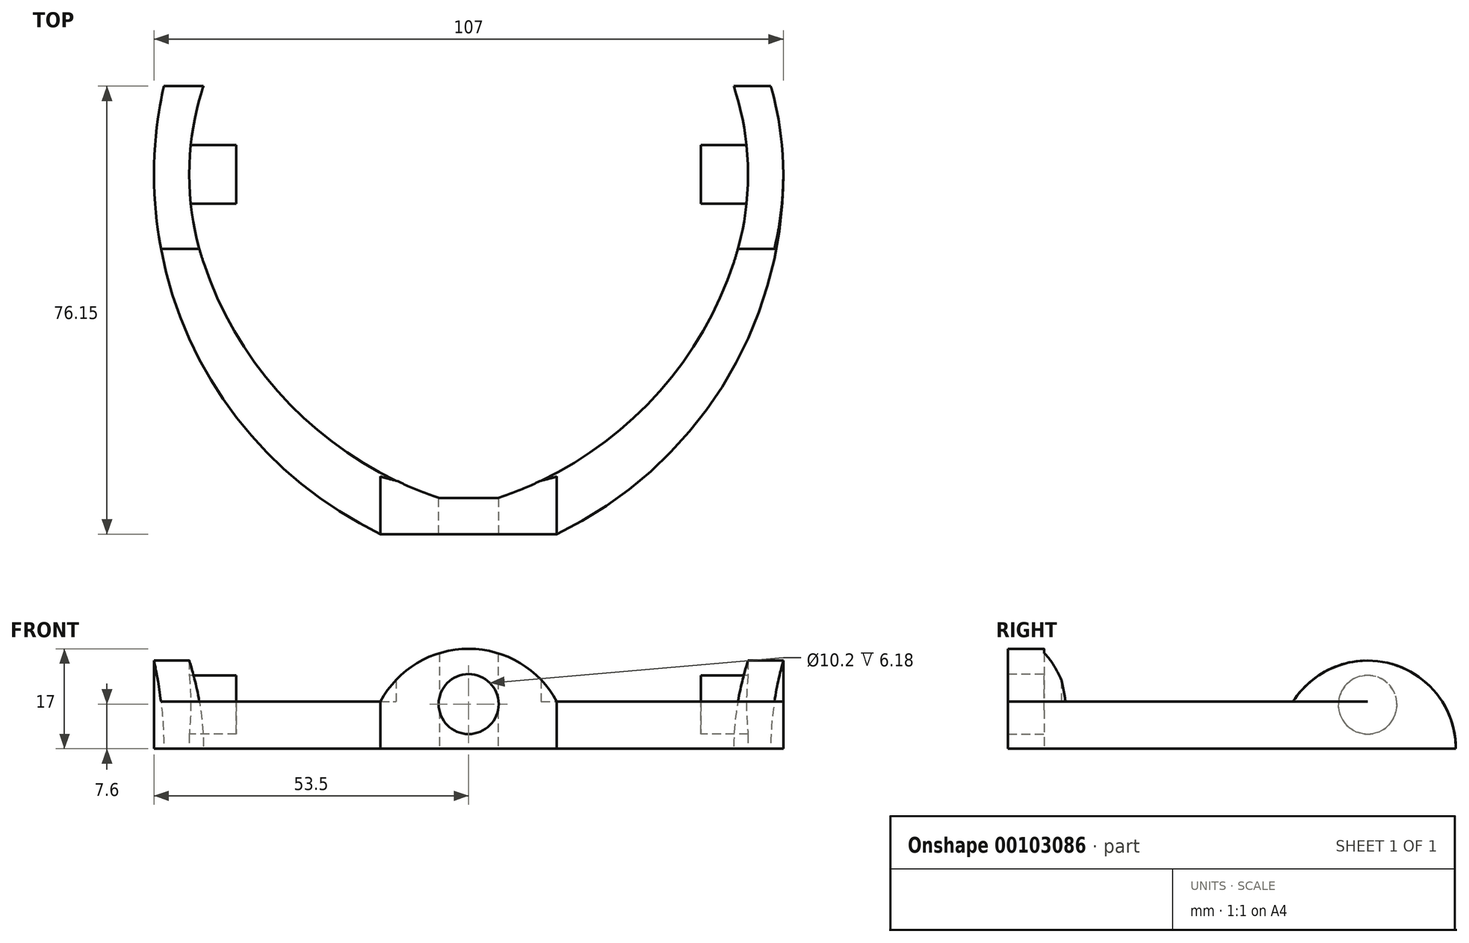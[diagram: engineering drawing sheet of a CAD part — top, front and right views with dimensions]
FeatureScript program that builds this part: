
annotation { "Feature Type Name" : "Feature", "Feature Type Description" : "" }
export const myFeature = defineFeature(function(context is Context, id is Id, definition is map)
    precondition{}
    {
        {
            var Q0;
            Q0=qCreatedBy(makeId("Top.planeOp"),FACE);
            var sketch = newSketch(context, id + "F0", { "sketchPlane" : qUnion([Q0])});
            skCircle(sketch, "E0", {"center": v(0, 0) * mm, "radius": 46 * mm});
            skCircle(sketch, "E1", {"center": v(0, 0) * mm, "radius": 40 * mm});
            skSolve(sketch);
        }
        {
            var Q0;
            Q0=qCreatedBy(makeId("Top.planeOp"),FACE);
            var sketch = newSketch(context, id + "F1", { "sketchPlane" : qUnion([Q0])});
            skArc(sketch, "E2.0", {"start": v(-45.07, 15) * mm, "mid": v(-47.5, 0) * mm, "end": v(-45.07, -15) * mm});
            skArc(sketch, "E3.0", {"start": v(-49.94, 19.18) * mm, "mid": v(-52.6, 9.75) * mm, "end": v(-53.5, 0) * mm});
            skLineSegment(sketch, "E4", {"start": v(0, 0) * mm, "end": v(0, -15) * mm, "construction": true});
            skLineSegment(sketch, "E5", {"start": v(-51.82, -15) * mm, "end": v(51.82, -15) * mm, "construction": true});
            skLineSegment(sketch, "E6", {"start": v(0, -55) * mm, "end": v(0, -65) * mm, "construction": true});
            skLineSegment(sketch, "E7", {"start": v(0, -65) * mm, "end": v(-5, -65) * mm});
            skLineSegment(sketch, "E8", {"start": v(0, -65) * mm, "end": v(5, -65) * mm});
            skArc(sketch, "E9", {"start": v(-53.5, 0) * mm, "mid": v(-53.08, -7.55) * mm, "end": v(-51.82, -15) * mm});
            skArc(sketch, "E10", {"start": v(5, -65) * mm, "mid": v(35.19, -46.35) * mm, "end": v(51.82, -15) * mm});
            skArc(sketch, "E11.trimOffspring", {"start": v(53.5, 0) * mm, "mid": v(52.6, 9.75) * mm, "end": v(49.94, 19.18) * mm});
            skLineSegment(sketch, "E12", {"start": v(-45.07, 15) * mm, "end": v(-49.94, 19.18) * mm});
            skLineSegment(sketch, "E13", {"start": v(45.07, 15) * mm, "end": v(49.94, 19.18) * mm});
            skLineSegment(sketch, "E14", {"start": v(-45.07, 15) * mm, "end": v(45.07, 15) * mm, "construction": true});
            skLineSegment(sketch, "E15", {"start": v(0, 0) * mm, "end": v(0, 15) * mm, "construction": true});
            skArc(sketch, "E16", {"start": v(-45.07, -15) * mm, "mid": v(0, -47.5) * mm, "end": v(45.07, -15) * mm, "construction": true});
            skArc(sketch, "E17", {"start": v(45.07, -15) * mm, "mid": v(47.5, 0) * mm, "end": v(45.07, 15) * mm});
            skArc(sketch, "E18", {"start": v(-51.82, -15) * mm, "mid": v(-35.19, -46.35) * mm, "end": v(-5, -65) * mm});
            skArc(sketch, "E19", {"start": v(51.82, -15) * mm, "mid": v(53.08, -7.55) * mm, "end": v(53.5, 0) * mm});
            skLineSegment(sketch, "E20", {"start": v(-5, -55) * mm, "end": v(0, -55) * mm});
            skLineSegment(sketch, "E21", {"start": v(0, -55) * mm, "end": v(5, -55) * mm});
            skArc(sketch, "E22", {"start": v(-45.07, -15) * mm, "mid": v(-29.77, -39.74) * mm, "end": v(-5, -55) * mm});
            skArc(sketch, "E23", {"start": v(5, -55) * mm, "mid": v(29.77, -39.74) * mm, "end": v(45.07, -15) * mm});
            skSolve(sketch);
        }
        {
            var Q0;
            Q0 = qSketchRegion(id + "F1", true);
            extrude(context, id + "F2", {"entities" : qUnion([Q0]), "depth" : 8 * mm});
        }
        {
            var Q0;
            Q0=qCreatedBy(makeId("Right.planeOp"),FACE);
            var sketch = newSketch(context, id + "F3", { "sketchPlane" : qUnion([Q0])});
            skArc(sketch, "E24", {"start": v(15, 0) * mm, "mid": v(0, 15) * mm, "end": v(-15, 0) * mm});
            skLineSegment(sketch, "E25", {"start": v(-15, 0) * mm, "end": v(15, 0) * mm});
            skSolve(sketch);
        }
        {
            var Q0;
            Q0 = qSketchRegion(id + "F3", true);
            var Q1;
            Q1=makeQuery(id+"F2.opExtrude","SWEPT_FACE",FACE,{"disambiguationData":[OSD([sQuery(id+"F1.wireOp",EDGE,"E9")])]});
            var Q2;
            Q2=makeQuery(id+"F2.opExtrude","SWEPT_FACE",FACE,{"disambiguationData":[OSD([sQuery(id+"F1.wireOp",EDGE,"E2.0")])]});
            extrude(context, id + "F4", {"entities" : qUnion([Q0]), "operationType" : NewBodyOperationType.ADD, "endBound" : BoundingType.UP_TO_SURFACE, "oppositeDirection" : true, "endBoundEntityFace" : qUnion([Q1]), "depth" : 25 * mm, "hasSecondDirection" : true, "secondDirectionBound" : SecondDirectionBoundingType.UP_TO_SURFACE, "secondDirectionOppositeDirection" : true, "secondDirectionBoundEntityFace" : qUnion([Q2]), "secondDirectionDepth" : 25 * mm});
        }
        {
            var Q0;
            Q0=qCreatedBy(makeId("Right.planeOp"),FACE);
            var sketch = newSketch(context, id + "F5", { "sketchPlane" : qUnion([Q0])});
            skArc(sketch, "E26", {"start": v(15, 0) * mm, "mid": v(0, 15) * mm, "end": v(-15, 0) * mm});
            skLineSegment(sketch, "E27", {"start": v(-15, 0) * mm, "end": v(15, 0) * mm});
            skSolve(sketch);
        }
        {
            var Q0;
            Q0 = qSketchRegion(id + "F5", true);
            var Q1;
            Q1=makeQuery(id+"F2.opExtrude","SWEPT_FACE",FACE,{"disambiguationData":[OSD([sQuery(id+"F1.wireOp",EDGE,"E11.trimOffspring")])]});
            var Q2;
            Q2=makeQuery(id+"F4.boolean.opBoolean","MERGE",FACE,{"derivedFrom":[makeQuery(id+"F2.opExtrude","SWEPT_FACE",FACE,{"disambiguationData":[OSD([sQuery(id+"F1.wireOp",EDGE,"E2.0")])]}),makeQuery(id+"F4.opExtrude","CAP_FACE",FACE,{"disambiguationData":[OSD([sQuery(id+"F3.wireOp",EDGE,"E24"),sQuery(id+"F3.wireOp",EDGE,"E25")]),OD(1.0)],"isStart":false})]});
            extrude(context, id + "F6", {"entities" : qUnion([Q0]), "operationType" : NewBodyOperationType.ADD, "endBound" : BoundingType.UP_TO_SURFACE, "endBoundEntityFace" : qUnion([Q1]), "depth" : 25 * mm, "hasSecondDirection" : true, "secondDirectionBound" : SecondDirectionBoundingType.UP_TO_SURFACE, "secondDirectionOppositeDirection" : false, "secondDirectionBoundEntityFace" : qUnion([Q2]), "secondDirectionDepth" : 25 * mm});
        }
        {
            var Q0;
            Q0=qCreatedBy(makeId("Right.planeOp"),FACE);
            var sketch = newSketch(context, id + "F7", { "sketchPlane" : qUnion([Q0])});
            skArc(sketch, "E28", {"start": v(15, 0) * mm, "mid": v(10.6, 10.6) * mm, "end": v(0, 15) * mm});
            skLineSegment(sketch, "E29", {"start": v(0, 15) * mm, "end": v(20.32, 15) * mm});
            skLineSegment(sketch, "E30", {"start": v(20.32, 15) * mm, "end": v(20.32, 0) * mm});
            skLineSegment(sketch, "E31", {"start": v(20.32, 0) * mm, "end": v(15, 0) * mm});
            skSolve(sketch);
        }
        {
            var Q0;
            Q0 = qSketchRegion(id + "F7", true);
            extrude(context, id + "F8", {"entities" : qUnion([Q0]), "operationType" : NewBodyOperationType.REMOVE, "endBound" : BoundingType.THROUGH_ALL, "oppositeDirection" : true, "depth" : 25 * mm, "hasSecondDirection" : true, "secondDirectionBound" : SecondDirectionBoundingType.THROUGH_ALL, "secondDirectionOppositeDirection" : false, "secondDirectionDepth" : 25 * mm});
        }
        {
            var Q0;
            Q0=qCreatedBy(makeId("Right.planeOp"),FACE);
            var sketch = newSketch(context, id + "F9", { "sketchPlane" : qUnion([Q0])});
            skCircle(sketch, "E32", {"center": v(0, 7.5) * mm, "radius": 5 * mm});
            skSolve(sketch);
        }
        {
            var Q0;
            Q0 = qSketchRegion(id + "F9", true);
            var Q1;
            Q1=makeQuery(id+"F6.boolean.opBoolean","MERGE",FACE,{"derivedFrom":[makeQuery(id+"F4.boolean.opBoolean","MERGE",FACE,{"derivedFrom":[makeQuery(id+"F2.opExtrude","SWEPT_FACE",FACE,{"disambiguationData":[OSD([sQuery(id+"F1.wireOp",EDGE,"E2.0")])]}),makeQuery(id+"F4.opExtrude","CAP_FACE",FACE,{"disambiguationData":[OSD([sQuery(id+"F3.wireOp",EDGE,"E24"),sQuery(id+"F3.wireOp",EDGE,"E25")]),OD(1.0)],"isStart":false})]}),makeQuery(id+"F6.opExtrude","CAP_FACE",FACE,{"disambiguationData":[OSD([sQuery(id+"F5.wireOp",EDGE,"E26"),sQuery(id+"F5.wireOp",EDGE,"E27")]),OD(0.0)],"isStart":false})]});
            var Q2;
            Q2=makeQuery(id+"F6.boolean.opBoolean","MERGE",FACE,{"derivedFrom":[makeQuery(id+"F4.boolean.opBoolean","MERGE",FACE,{"derivedFrom":[makeQuery(id+"F2.opExtrude","SWEPT_FACE",FACE,{"disambiguationData":[OSD([sQuery(id+"F1.wireOp",EDGE,"E2.0")])]}),makeQuery(id+"F4.opExtrude","CAP_FACE",FACE,{"disambiguationData":[OSD([sQuery(id+"F3.wireOp",EDGE,"E24"),sQuery(id+"F3.wireOp",EDGE,"E25")]),OD(1.0)],"isStart":false})]}),makeQuery(id+"F6.opExtrude","CAP_FACE",FACE,{"disambiguationData":[OSD([sQuery(id+"F5.wireOp",EDGE,"E26"),sQuery(id+"F5.wireOp",EDGE,"E27")]),OD(0.0)],"isStart":false})]});
            extrude(context, id + "F10", {"entities" : qUnion([Q0]), "operationType" : NewBodyOperationType.ADD, "endBound" : BoundingType.UP_TO_SURFACE, "endBoundEntityFace" : qUnion([Q1]), "depth" : 25 * mm, "hasSecondDirection" : true, "secondDirectionBound" : SecondDirectionBoundingType.UP_TO_SURFACE, "secondDirectionOppositeDirection" : true, "secondDirectionBoundEntityFace" : qUnion([Q2]), "secondDirectionDepth" : 25 * mm});
        }
        {
            var Q0;
            Q0=qCreatedBy(makeId("Top.planeOp"),FACE);
            var sketch = newSketch(context, id + "F11", { "sketchPlane" : qUnion([Q0])});
            skLineSegment(sketch, "E33.bottom", {"start": v(39.5, -13.07) * mm, "end": v(-39.5, -13.07) * mm});
            skLineSegment(sketch, "E33.top", {"start": v(39.5, 13.07) * mm, "end": v(-39.5, 13.07) * mm});
            skLineSegment(sketch, "E33.left", {"start": v(39.5, -13.07) * mm, "end": v(39.5, 13.07) * mm});
            skLineSegment(sketch, "E33.right", {"start": v(-39.5, -13.07) * mm, "end": v(-39.5, 13.07) * mm});
            skPoint(sketch, "E33.middle", {"position": v(0, 0) * mm});
            skSolve(sketch);
        }
        {
            var Q0;
            Q0 = qSketchRegion(id + "F11", true);
            extrude(context, id + "F12", {"entities" : qUnion([Q0]), "operationType" : NewBodyOperationType.REMOVE, "endBound" : BoundingType.THROUGH_ALL, "depth" : 25 * mm});
        }
        {
            var Q0;
            Q0=qCreatedBy(makeId("Front.planeOp"),FACE);
            var sketch = newSketch(context, id + "F13", { "sketchPlane" : qUnion([Q0])});
            skArc(sketch, "E34", {"start": v(17, 0) * mm, "mid": v(0, 17) * mm, "end": v(-17, 0) * mm});
            skLineSegment(sketch, "E35", {"start": v(-17, 0) * mm, "end": v(17, 0) * mm});
            skSolve(sketch);
        }
        {
            var Q0;
            Q0 = qSketchRegion(id + "F13", true);
            var Q1;
            {var subQ0=sQuery(id+"F1.wireOp",EDGE,"E10");var subQ1=sQuery(id+"F3.wireOp",EDGE,"E25");var subQ2=sQuery(id+"F1.wireOp",EDGE,"E9");var subQ3=sQuery(id+"F1.wireOp",EDGE,"E8");var subQ4=sQuery(id+"F1.wireOp",EDGE,"E7");Q1=makeQuery(id+"F16.boolean.opBoolean","SPLIT",FACE,{"disambiguationData":[TD([makeQuery(id+"F2.opExtrude","CAP_FACE",FACE,{"disambiguationData":[OSD([sQuery(id+"F1.wireOp",EDGE,"E2.0"),sQuery(id+"F1.wireOp",EDGE,"E3.0"),subQ4,subQ3,subQ2,subQ0,sQuery(id+"F1.wireOp",EDGE,"E11.trimOffspring"),sQuery(id+"F1.wireOp",EDGE,"E12"),sQuery(id+"F1.wireOp",EDGE,"E13")])],"isStart":true}),makeQuery(id+"F2.opExtrude","SWEPT_FACE",FACE,{"disambiguationData":[OSD([subQ2])]}),makeQuery(id+"F2.opExtrude","SWEPT_FACE",FACE,{"disambiguationData":[OSD([subQ0])]}),makeQuery(id+"F4.opExtrude","SWEPT_FACE",FACE,{"disambiguationData":[OSD([subQ1])]}),makeQuery(id+"F4.opExtrude","CAP_FACE",FACE,{"disambiguationData":[OSD([sQuery(id+"F3.wireOp",EDGE,"E24"),subQ1]),OD(0.0)],"isStart":false}),makeQuery(id+"F16.opExtrude","SWEPT_FACE",FACE,{"disambiguationData":[OSD([sQuery(id+"F15.wireOp",EDGE,"E36")])]})])],"derivedFrom":makeQuery(id+"F2.opExtrude","SWEPT_FACE",FACE,{"disambiguationData":[OSD([subQ4,subQ3])]})});}
            var Q2;
            Q2=makeQuery(id+"F6.boolean.opBoolean","MERGE",FACE,{"derivedFrom":[makeQuery(id+"F4.boolean.opBoolean","MERGE",FACE,{"derivedFrom":[makeQuery(id+"F2.opExtrude","SWEPT_FACE",FACE,{"disambiguationData":[OSD([sQuery(id+"F1.wireOp",EDGE,"E2.0")])]}),makeQuery(id+"F4.opExtrude","CAP_FACE",FACE,{"disambiguationData":[OSD([sQuery(id+"F3.wireOp",EDGE,"E24"),sQuery(id+"F3.wireOp",EDGE,"E25")]),OD(1.0)],"isStart":false})]}),makeQuery(id+"F6.opExtrude","CAP_FACE",FACE,{"disambiguationData":[OSD([sQuery(id+"F5.wireOp",EDGE,"E26"),sQuery(id+"F5.wireOp",EDGE,"E27")]),OD(0.0)],"isStart":false})]});
            extrude(context, id + "F14", {"entities" : qUnion([Q0]), "operationType" : NewBodyOperationType.ADD, "endBound" : BoundingType.UP_TO_SURFACE, "endBoundEntityFace" : qUnion([Q1]), "depth" : 25 * mm, "hasSecondDirection" : true, "secondDirectionBound" : SecondDirectionBoundingType.UP_TO_SURFACE, "secondDirectionOppositeDirection" : false, "secondDirectionBoundEntityFace" : qUnion([Q2]), "secondDirectionDepth" : 25 * mm});
        }
        {
            var Q0;
            Q0=qCreatedBy(makeId("Front.planeOp"),FACE);
            var sketch = newSketch(context, id + "F15", { "sketchPlane" : qUnion([Q0])});
            skCircle(sketch, "E36", {"center": v(0, 7.6) * mm, "radius": 5.1 * mm});
            skSolve(sketch);
        }
        {
            var Q0;
            Q0 = qSketchRegion(id + "F15", true);
            extrude(context, id + "F16", {"entities" : qUnion([Q0]), "operationType" : NewBodyOperationType.REMOVE, "endBound" : BoundingType.THROUGH_ALL, "depth" : 25 * mm});
        }
        {
            var Q0;
            Q0=qCreatedBy(makeId("Top.planeOp"),FACE);
            var sketch = newSketch(context, id + "F17", { "sketchPlane" : qUnion([Q0])});
            skArc(sketch, "E37.0", {"start": v(-52.3, -12.69) * mm, "mid": v(-39.42, -41.36) * mm, "end": v(-15, -61.15) * mm});
            skArc(sketch, "E38.0", {"start": v(15, -61.15) * mm, "mid": v(43.07, -36.13) * mm, "end": v(53.5, 0) * mm});
            skLineSegment(sketch, "E39", {"start": v(-52.3, -12.69) * mm, "end": v(-52.3, -67.22) * mm});
            skLineSegment(sketch, "E40", {"start": v(-52.3, -67.22) * mm, "end": v(53.5, -67.22) * mm});
            skLineSegment(sketch, "E41", {"start": v(53.5, -67.22) * mm, "end": v(53.5, 0) * mm});
            skLineSegment(sketch, "E42", {"start": v(-15, -61.15) * mm, "end": v(15, -61.15) * mm});
            skSolve(sketch);
        }
        {
            var Q0;
            Q0 = qSketchRegion(id + "F17", true);
            extrude(context, id + "F18", {"entities" : qUnion([Q0]), "operationType" : NewBodyOperationType.REMOVE, "endBound" : BoundingType.THROUGH_ALL, "depth" : 25 * mm});
        }
        {
            var Q0;
            Q0=makeQuery(id+"F1.imprint","IMPRINT",FACE,{"disambiguationData":[TD([[makeQuery(id+"F1.imprint","IMPRINT",EDGE,{"derivedFrom":sQuery(id+"F1.wireOp",EDGE,"E2.0")}),-1.0]])]});
            var sketch = newSketch(context, id + "F19", { "sketchPlane" : qUnion([Q0])});
            skArc(sketch, "E43.0", {"start": v(-45.07, -15) * mm, "mid": v(-29.77, -39.74) * mm, "end": v(-5, -55) * mm});
            skLineSegment(sketch, "E43.1", {"start": v(-5, -55) * mm, "end": v(0, -55) * mm});
            skLineSegment(sketch, "E43.2", {"start": v(0, -55) * mm, "end": v(5, -55) * mm});
            skArc(sketch, "E43.3", {"start": v(5, -55) * mm, "mid": v(29.77, -39.74) * mm, "end": v(45.07, -15) * mm});
            skLineSegment(sketch, "E44", {"start": v(-45.07, -15) * mm, "end": v(45.07, -15) * mm});
            skSolve(sketch);
        }
        {
            var Q0;
            Q0 = qSketchRegion(id + "F19", true);
            extrude(context, id + "F20", {"entities" : qUnion([Q0]), "operationType" : NewBodyOperationType.REMOVE, "endBound" : BoundingType.THROUGH_ALL, "depth" : 25 * mm});
        }
    });
